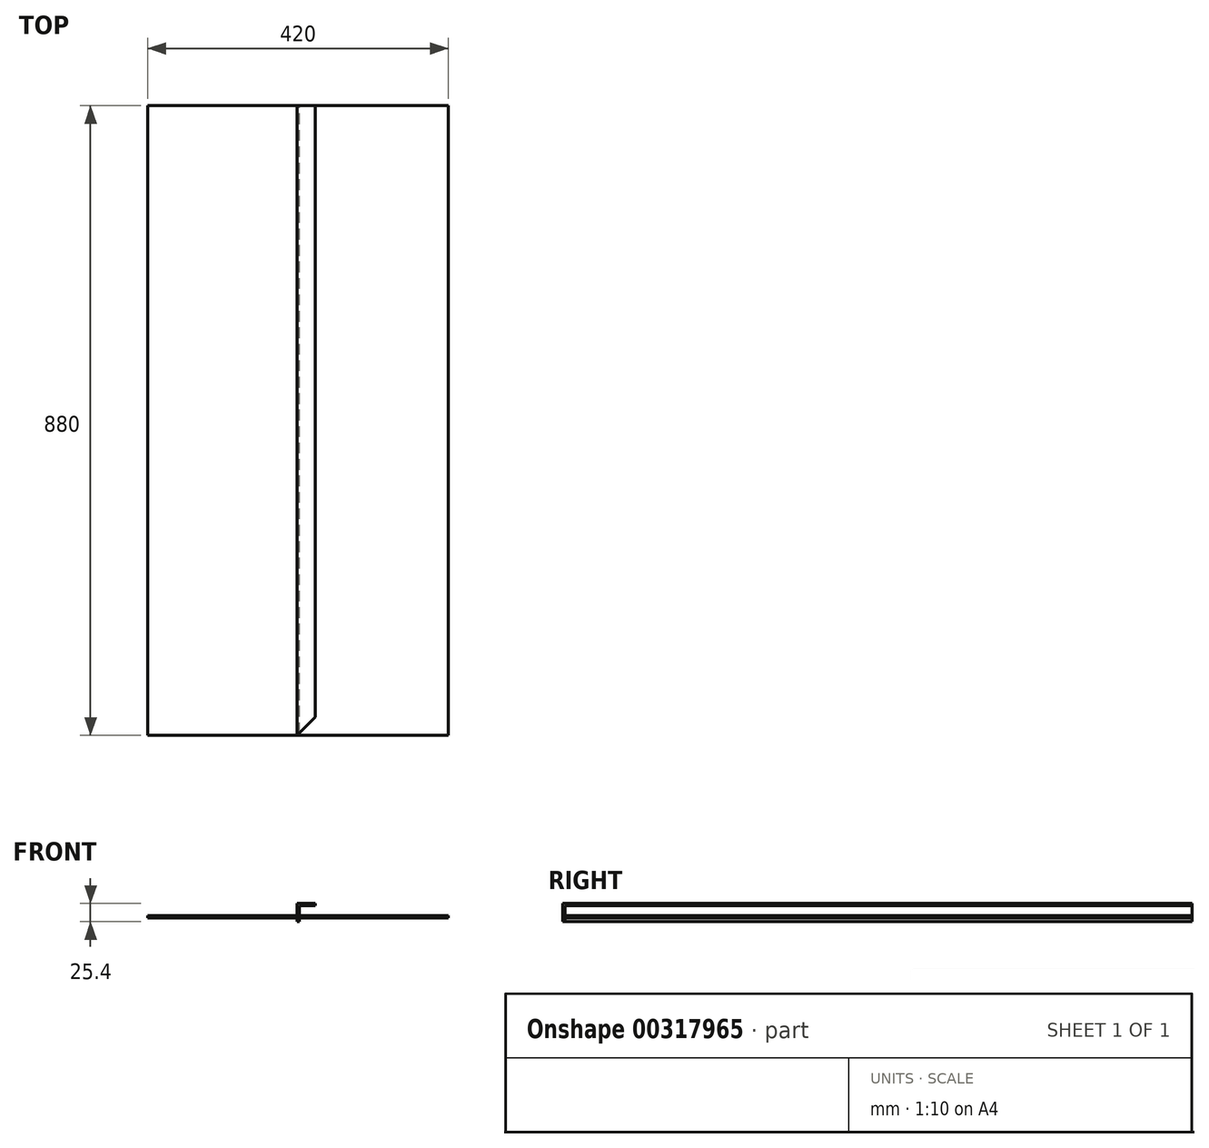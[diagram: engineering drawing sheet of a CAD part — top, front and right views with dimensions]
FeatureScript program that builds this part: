
annotation { "Feature Type Name" : "Feature", "Feature Type Description" : "" }
export const myFeature = defineFeature(function(context is Context, id is Id, definition is map)
    precondition{}
    {
        {
            var Q0;
            Q0=qCreatedBy(makeId("Front.planeOp"),FACE);
            var sketch = newSketch(context, id + "F0", { "sketchPlane" : qUnion([Q0])});
            skLineSegment(sketch, "E0.0", {"start": v(1.6, 15.16) * mm, "end": v(23.8, 15.16) * mm});
            skLineSegment(sketch, "E0.1", {"start": v(1.6, -7.04) * mm, "end": v(1.6, 15.16) * mm});
            skLineSegment(sketch, "E1.0", {"start": v(-1.6, 18.36) * mm, "end": v(23.8, 18.36) * mm});
            skLineSegment(sketch, "E1.1", {"start": v(-1.6, -7.04) * mm, "end": v(-1.6, 18.36) * mm});
            skLineSegment(sketch, "E2", {"start": v(-1.6, -7.04) * mm, "end": v(1.6, -7.04) * mm});
            skPoint(sketch, "E3.orphan", {"position": v(0, -8.64) * mm});
            skLineSegment(sketch, "E4", {"start": v(23.8, 18.36) * mm, "end": v(23.8, 15.16) * mm});
            skSolve(sketch);
        }
        {
            var Q0;
            Q0 = qSketchRegion(id + "F0", true);
            extrude(context, id + "F1", {"entities" : qUnion([Q0]), "endBound" : BoundingType.SYMMETRIC, "depth" : 880 * mm});
        }
        {
            var Q0;
            Q0=makeQuery(id+"F1.opExtrude","SWEPT_FACE",FACE,{"disambiguationData":[OSD([sQuery(id+"F0.wireOp",EDGE,"E1.0")])]});
            var sketch = newSketch(context, id + "F2", { "sketchPlane" : qUnion([Q0])});
            skLineSegment(sketch, "E5", {"start": v(-1.6, -440) * mm, "end": v(23.8, -414.6) * mm});
            skLineSegment(sketch, "E6", {"start": v(-1.6, -440) * mm, "end": v(-1.6, -411.89) * mm});
            skLineSegment(sketch, "E7", {"start": v(23.8, -414.6) * mm, "end": v(23.8, -440) * mm});
            skLineSegment(sketch, "E8", {"start": v(23.8, -440) * mm, "end": v(-1.6, -440) * mm});
            skSolve(sketch);
        }
        {
            var Q0;
            Q0 = qSketchRegion(id + "F2", true);
            extrude(context, id + "F3", {"entities" : qUnion([Q0]), "operationType" : NewBodyOperationType.REMOVE, "oppositeDirection" : true, "depth" : 25.4 * mm});
        }
        {
            var Q0;
            Q0=qCreatedBy(makeId("Top.planeOp"),FACE);
            var sketch = newSketch(context, id + "F4", { "sketchPlane" : qUnion([Q0])});
            skLineSegment(sketch, "E9.bottom", {"start": v(210, 440) * mm, "end": v(-210, 440) * mm});
            skLineSegment(sketch, "E9.top", {"start": v(210, -440) * mm, "end": v(-210, -440) * mm});
            skLineSegment(sketch, "E9.left", {"start": v(210, 440) * mm, "end": v(210, -440) * mm});
            skLineSegment(sketch, "E9.right", {"start": v(-210, 440) * mm, "end": v(-210, -440) * mm});
            skPoint(sketch, "E9.middle", {"position": v(0, 0) * mm});
            skSolve(sketch);
        }
        {
            var Q0;
            Q0 = qSketchRegion(id + "F4", true);
            extrude(context, id + "F5", {"entities" : qUnion([Q0]), "endBound" : BoundingType.SYMMETRIC, "depth" : 3 * mm});
        }
    });
